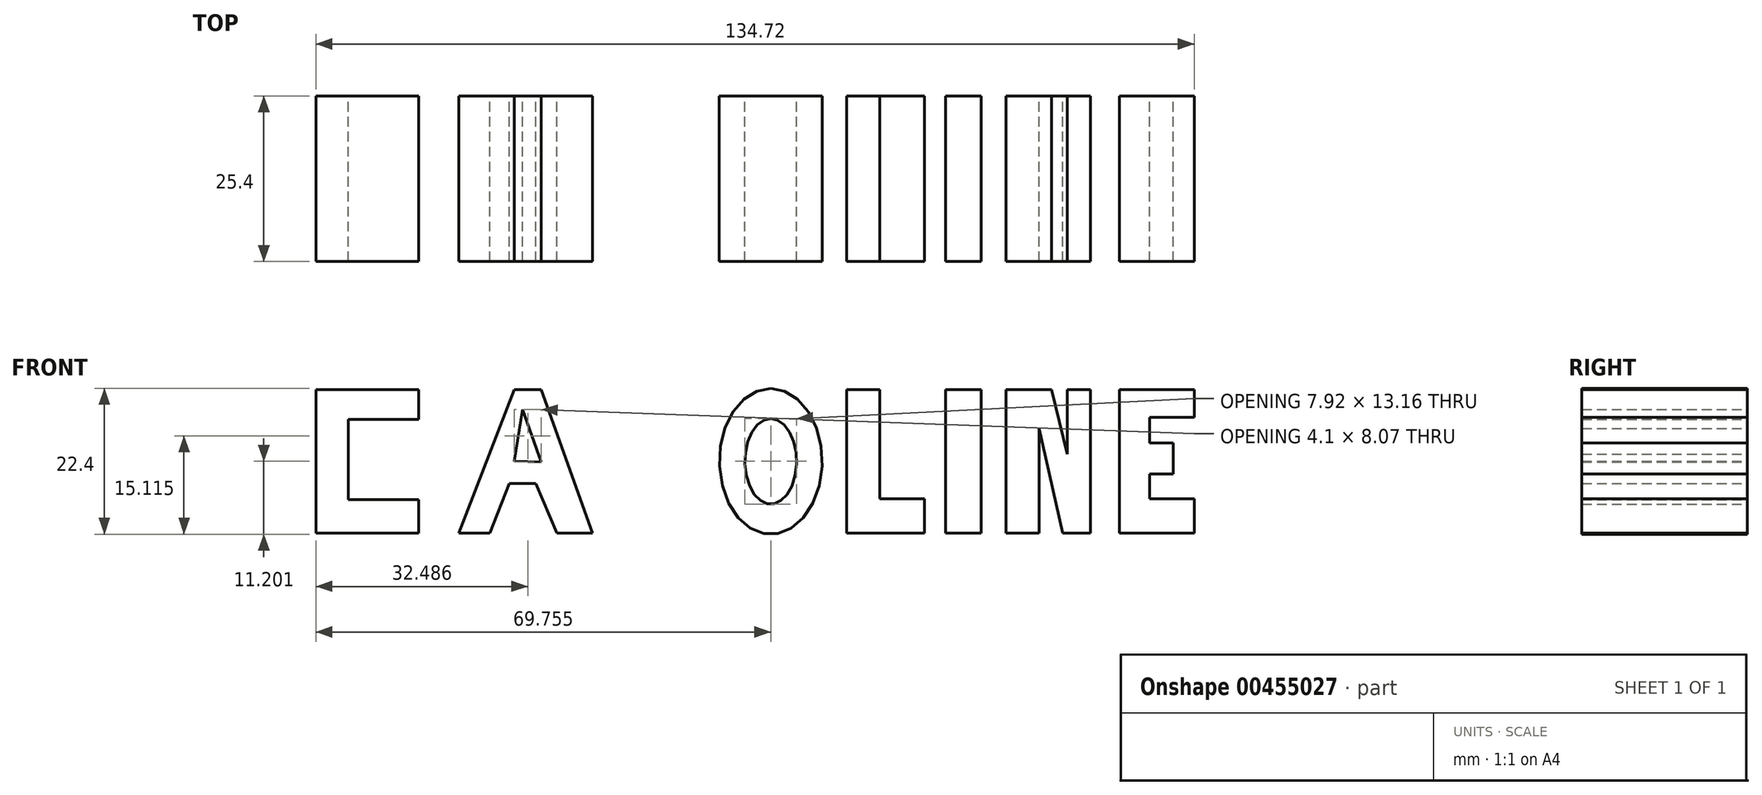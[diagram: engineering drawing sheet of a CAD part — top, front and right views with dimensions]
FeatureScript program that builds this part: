
annotation { "Feature Type Name" : "Feature", "Feature Type Description" : "" }
export const myFeature = defineFeature(function(context is Context, id is Id, definition is map)
    precondition{}
    {
        {
            var Q0;
            Q0=qCreatedBy(makeId("Front.planeOp"),FACE);
            var sketch = newSketch(context, id + "F0", { "sketchPlane" : qUnion([Q0])});
            skLineSegment(sketch, "E0", {"start": v(-47.7, 51.29) * mm, "end": v(-63.43, 51.29) * mm});
            skLineSegment(sketch, "E1", {"start": v(-63.43, 51.29) * mm, "end": v(-63.43, 29.23) * mm});
            skLineSegment(sketch, "E2", {"start": v(-63.43, 29.23) * mm, "end": v(-47.7, 29.23) * mm});
            skLineSegment(sketch, "E3", {"start": v(-47.7, 29.23) * mm, "end": v(-47.7, 34.36) * mm});
            skLineSegment(sketch, "E4", {"start": v(-47.7, 34.36) * mm, "end": v(-58.47, 34.36) * mm});
            skLineSegment(sketch, "E5", {"start": v(-58.47, 34.36) * mm, "end": v(-58.47, 46.67) * mm});
            skLineSegment(sketch, "E6", {"start": v(-58.47, 46.67) * mm, "end": v(-47.7, 46.67) * mm});
            skLineSegment(sketch, "E7", {"start": v(-47.7, 51.29) * mm, "end": v(-47.7, 46.67) * mm});
            skLineSegment(sketch, "E8", {"start": v(-33, 51.29) * mm, "end": v(-41.54, 29.23) * mm});
            skLineSegment(sketch, "E9", {"start": v(-41.54, 29.23) * mm, "end": v(-36.76, 29.23) * mm});
            skLineSegment(sketch, "E10", {"start": v(-36.76, 29.23) * mm, "end": v(-33.8, 36.88) * mm});
            skLineSegment(sketch, "E11", {"start": v(-33.8, 36.88) * mm, "end": v(-29.75, 36.88) * mm});
            skLineSegment(sketch, "E12", {"start": v(-29.75, 36.88) * mm, "end": v(-26.5, 29.23) * mm});
            skLineSegment(sketch, "E13", {"start": v(-26.5, 29.23) * mm, "end": v(-21.03, 29.23) * mm});
            skLineSegment(sketch, "E14", {"start": v(-21.03, 29.23) * mm, "end": v(-28.9, 51.29) * mm});
            skLineSegment(sketch, "E15", {"start": v(-28.9, 51.29) * mm, "end": v(-33, 51.29) * mm});
            skLineSegment(sketch, "E16", {"start": v(-33, 40.26) * mm, "end": v(-31.77, 48.21) * mm});
            skPoint(sketch, "E16.startSnap0", {"position": v(-37.27, 40.26) * mm});
            skPoint(sketch, "E16.endSnap0", {"position": v(-31.77, 36.88) * mm});
            skLineSegment(sketch, "E17", {"start": v(-31.77, 48.21) * mm, "end": v(-28.9, 40.14) * mm});
            skLineSegment(sketch, "E18", {"start": v(-28.9, 40.14) * mm, "end": v(-33, 40.26) * mm});
            skLineSegment(sketch, "E19", {"start": v(-16.58, 51.29) * mm, "end": v(-16.58, 29.23) * mm});
            skLineSegment(sketch, "E20", {"start": v(-16.58, 29.23) * mm, "end": v(-12.65, 29.23) * mm});
            skLineSegment(sketch, "E21", {"start": v(-12.65, 29.23) * mm, "end": v(-12.65, 40.26) * mm});
            skLineSegment(sketch, "E22", {"start": v(-12.65, 40.26) * mm, "end": v(-7.97, 29.23) * mm});
            skLineSegment(sketch, "E23", {"start": v(-7.97, 29.23) * mm, "end": v(-3.76, 29.23) * mm});
            skLineSegment(sketch, "E24", {"start": v(-3.76, 29.23) * mm, "end": v(-9.14, 41.9) * mm});
            skLineSegment(sketch, "E25", {"start": v(-9.14, 51.29) * mm, "end": v(-16.58, 51.29) * mm});
            skLineSegment(sketch, "E26", {"start": v(-12.65, 48.55) * mm, "end": v(-12.65, 44.8) * mm});
            skLineSegment(sketch, "E27", {"start": v(17.95, 51.29) * mm, "end": v(17.95, 29.23) * mm});
            skLineSegment(sketch, "E28", {"start": v(17.95, 29.23) * mm, "end": v(29.92, 29.23) * mm});
            skLineSegment(sketch, "E29", {"start": v(29.92, 29.23) * mm, "end": v(29.92, 34.53) * mm});
            skLineSegment(sketch, "E30", {"start": v(29.92, 34.53) * mm, "end": v(23.08, 34.53) * mm});
            skLineSegment(sketch, "E31", {"start": v(23.08, 34.53) * mm, "end": v(23.08, 51.29) * mm});
            skLineSegment(sketch, "E32", {"start": v(23.08, 51.29) * mm, "end": v(17.95, 51.29) * mm});
            skLineSegment(sketch, "E33", {"start": v(33.17, 51.29) * mm, "end": v(33.17, 29.23) * mm});
            skLineSegment(sketch, "E34", {"start": v(33.17, 29.23) * mm, "end": v(38.64, 29.23) * mm});
            skLineSegment(sketch, "E35", {"start": v(38.64, 29.23) * mm, "end": v(38.64, 51.29) * mm});
            skLineSegment(sketch, "E36", {"start": v(38.64, 51.29) * mm, "end": v(33.17, 51.29) * mm});
            skLineSegment(sketch, "E37", {"start": v(42.4, 51.29) * mm, "end": v(42.4, 29.23) * mm});
            skLineSegment(sketch, "E38", {"start": v(42.4, 29.23) * mm, "end": v(47.53, 29.23) * mm});
            skLineSegment(sketch, "E39", {"start": v(47.53, 29.23) * mm, "end": v(47.53, 45.3) * mm});
            skLineSegment(sketch, "E40", {"start": v(47.53, 45.3) * mm, "end": v(51.12, 29.23) * mm});
            skLineSegment(sketch, "E41", {"start": v(51.12, 29.23) * mm, "end": v(55.4, 29.23) * mm});
            skLineSegment(sketch, "E42", {"start": v(55.4, 29.23) * mm, "end": v(55.4, 51.29) * mm});
            skLineSegment(sketch, "E43", {"start": v(55.4, 51.29) * mm, "end": v(51.8, 51.29) * mm});
            skLineSegment(sketch, "E44", {"start": v(51.8, 51.29) * mm, "end": v(51.8, 41.37) * mm});
            skLineSegment(sketch, "E45", {"start": v(51.8, 41.37) * mm, "end": v(49.4, 51.29) * mm});
            skLineSegment(sketch, "E46", {"start": v(49.4, 51.29) * mm, "end": v(42.4, 51.29) * mm});
            skLineSegment(sketch, "E47", {"start": v(59.84, 51.29) * mm, "end": v(59.84, 29.23) * mm});
            skLineSegment(sketch, "E48", {"start": v(59.84, 29.23) * mm, "end": v(71.3, 29.23) * mm});
            skLineSegment(sketch, "E49", {"start": v(71.3, 29.23) * mm, "end": v(71.3, 34.53) * mm});
            skLineSegment(sketch, "E50", {"start": v(71.3, 34.53) * mm, "end": v(64.45, 34.53) * mm});
            skLineSegment(sketch, "E51", {"start": v(64.45, 34.53) * mm, "end": v(64.45, 38.3) * mm});
            skLineSegment(sketch, "E52", {"start": v(64.45, 38.3) * mm, "end": v(68.04, 38.3) * mm});
            skLineSegment(sketch, "E53", {"start": v(68.04, 38.3) * mm, "end": v(68.04, 43.08) * mm});
            skLineSegment(sketch, "E54", {"start": v(68.04, 43.08) * mm, "end": v(64.45, 43.08) * mm});
            skLineSegment(sketch, "E55", {"start": v(64.45, 43.08) * mm, "end": v(64.45, 47.01) * mm});
            skLineSegment(sketch, "E56", {"start": v(64.45, 47.01) * mm, "end": v(71.3, 47.01) * mm});
            skLineSegment(sketch, "E57", {"start": v(71.3, 47.01) * mm, "end": v(71.3, 51.29) * mm});
            skLineSegment(sketch, "E58", {"start": v(59.84, 51.29) * mm, "end": v(71.3, 51.29) * mm});
            skArc(sketch, "E59", {"start": v(-12.65, 48.55) * mm, "mid": v(-10.77, 46.67) * mm, "end": v(-12.65, 44.8) * mm});
            skArc(sketch, "E60", {"start": v(-9.14, 51.29) * mm, "mid": v(-5.88, 46.82) * mm, "end": v(-8.87, 42.16) * mm});
            skEllipse(sketch, "E61", {"center": v(6.33, 40.26) * mm, "majorRadius": 11.2 * mm, "minorRadius": 7.9 * mm, "majorAxis": v(0, 1)});
            skPoint(sketch, "E61.centerSnap0", {"position": v(-16.58, 40.26) * mm});
            skEllipse(sketch, "E62", {"center": v(6.33, 40.26) * mm, "majorRadius": 6.58 * mm, "minorRadius": 3.96 * mm, "majorAxis": v(0, 1)});
            skSolve(sketch);
        }
        {
            var Q0;
            Q0=makeQuery(id+"F0.imprint","IMPRINT",FACE,{"disambiguationData":[TD([[makeQuery(id+"F0.imprint","IMPRINT",EDGE,{"derivedFrom":sQuery(id+"F0.wireOp",EDGE,"E0")}),1.0]])]});
            var Q1;
            Q1=makeQuery(id+"F0.imprint","IMPRINT",FACE,{"disambiguationData":[TD([[makeQuery(id+"F0.imprint","IMPRINT",EDGE,{"derivedFrom":sQuery(id+"F0.wireOp",EDGE,"E27")}),1.0]])]});
            var Q2;
            Q2=makeQuery(id+"F0.imprint","IMPRINT",FACE,{"disambiguationData":[TD([[makeQuery(id+"F0.imprint","IMPRINT",EDGE,{"derivedFrom":sQuery(id+"F0.wireOp",EDGE,"E33")}),1.0]])]});
            var Q3;
            Q3=makeQuery(id+"F0.imprint","IMPRINT",FACE,{"disambiguationData":[TD([[makeQuery(id+"F0.imprint","IMPRINT",EDGE,{"derivedFrom":sQuery(id+"F0.wireOp",EDGE,"E37")}),1.0]])]});
            var Q4;
            Q4=makeQuery(id+"F0.imprint","IMPRINT",FACE,{"disambiguationData":[TD([[makeQuery(id+"F0.imprint","IMPRINT",EDGE,{"derivedFrom":sQuery(id+"F0.wireOp",EDGE,"E47")}),1.0]])]});
            var Q5;
            Q5=makeQuery(id+"F0.imprint","IMPRINT",FACE,{"disambiguationData":[TD([[makeQuery(id+"F0.imprint","IMPRINT",EDGE,{"derivedFrom":sQuery(id+"F0.wireOp",EDGE,"E61")}),1.0]])]});
            var Q6;
            Q6=makeQuery(id+"F0.imprint","IMPRINT",FACE,{"disambiguationData":[TD([[makeQuery(id+"F0.imprint","IMPRINT",EDGE,{"derivedFrom":sQuery(id+"F0.wireOp",EDGE,"E8")}),1.0]])]});
            extrude(context, id + "F1", {"entities" : qUnion([Q0, Q1, Q2, Q3, Q4, Q5, Q6]), "depth" : 25.4 * mm});
        }
    });
